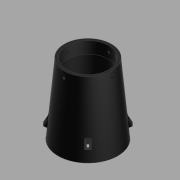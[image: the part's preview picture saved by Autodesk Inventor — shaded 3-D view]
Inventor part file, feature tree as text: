
AUTODESK INVENTOR PART (.ipt)
format: ipt  version: 2020 (Build 240168000, 168)  size: 985,088 bytes
history: native  units: mm
features: sketch x12, other x10, extrude x8, pattern_circular x4, revolve x3, plane x2, fillet x2, projected_geometry x2, loft x1
ambient origin geometry x8: Origin, YZ Plane, XZ Plane, XY Plane, X Axis, Y Axis, Z Axis, Center Point
bodies: Solid1 (feature_tree), Solid2 (feature_tree), Solid3 (feature_tree), Solid4 (feature_tree)
feature tree (44):
  other  "Mounted Camera w Lens.iam"
  other  "Camera Mount 01.ipt:1"
  other  "Spinel USB Camera 01 trimmed.ipt:1"
  other  "M12 2.8-12mm F1.4 Lens.ipt:1"
  other  "WellTop"
  other  "CamYZ"
  other  "CamXY"
  other  "PipetteCutOff"
  other  "CamCenterLine"
  revolve  "Revolution1"  [1 undecoded]
  other  "LEDPlane"
  plane  "Work Plane7"
  sketch  "Sketch2"  dims[d0=10.0mm d1=40.0mm]
  extrude  "Extrusion11"  Depth=30.0mm
  extrude  "Extrusion12"  TaperAngle=90.0deg  [1 undecoded]
  extrude  "Extrusion13"  Depth=2.0mm
  extrude  "Extrusion14"  Depth=4.18879mm
  fillet  "Fillet1"  Radius=2.96706mm
  fillet  "Fillet2"  Radius=0.25mm
  pattern_circular  "Circular Pattern2"  [2 undecoded]
  extrude  "Extrusion15"  Depth=0.5mm
  pattern_circular  "Circular Pattern3"  [2 undecoded]
  revolve  "Revolution2"  [1 undecoded]
  pattern_circular  "Circular Pattern4"  [2 undecoded]
  revolve  "Revolution3"  [1 undecoded]
  sketch  "Sketch20"  dims[d72=11.021731mm]
  plane  "Work Plane9"
  loft  "Loft1"
  pattern_circular  "Circular Pattern5"  [2 undecoded]
  extrude  "Extrusion16"  Depth=0.5mm
  extrude  "Extrusion17"  Depth=0.5mm TaperAngle=0.0deg
  extrude  "Extrusion18"  Depth=0.5mm
  sketch  "Sketch12"  dims[d6=8.0mm d7=30.0mm]
  sketch  "Sketch14"  dims[d8=2.5mm d9=90.0deg]
  sketch  "Sketch15"  dims[d10=1.5mm d18=2.0mm]
  sketch  "Sketch16"  dims[d21=5.934119mm d23=4.18879mm d25=2.96706mm d66=0.25mm]
  sketch  "Sketch17"  dims[d69=17.65mm]
  sketch  "Sketch18"  dims[d70=35.71mm]
  sketch  "Sketch19"  dims[d71=11.021731mm]
  projected_geometry  "Projected Loop5"
  projected_geometry  "Projected Loop6"
  sketch  "Sketch21"  dims[d73=8.968224mm]
  sketch  "Sketch22"  dims[d74=2.1mm]
  sketch  "Sketch23"  dims[d75=2.1mm d76=4.18879mm d77=3.15mm d78=0.933mm d79=0.5mm d80=3.3mm d81=0.0mm d82=0.5mm d83=5.0mm d84=0.5mm d85=0.5mm d86=2.8mm d87=0.0mm d88=0.5mm d89=1.6mm d90=1.6mm d91=2.3mm d92=0.35mm d93=2.8mm d94=0.0mm d95=0.5mm d96=0.5mm d97=2.25mm d98=0.5mm d99=0.0mm d100=0.5mm d101=0.25mm d102=40.0mm d103=360.0deg d105=1.5mm d106=45.0mm d107=0.0mm d108=20.0mm d109=90.0deg d111=14.137167mm d112=40.0mm d113=360.0deg d115=14.137167mm d116=1.745329mm d117=3.5mm d118=1.6mm d121=0.0mm d122=90.0deg d123=0.0mm d124=90.0deg d125=40.0mm d126=360.0deg d128=45.0mm d129=0.0mm d130=0.5mm d131=0.0mm d132=0.5mm d133=0.0mm d67=0.5mm d68=0.872665mm]
note: 12 required parameter values undecoded (feature->parameter linkage not recoverable at this tier; creation-order binding heuristic only, values carry confidence <= 0.55)